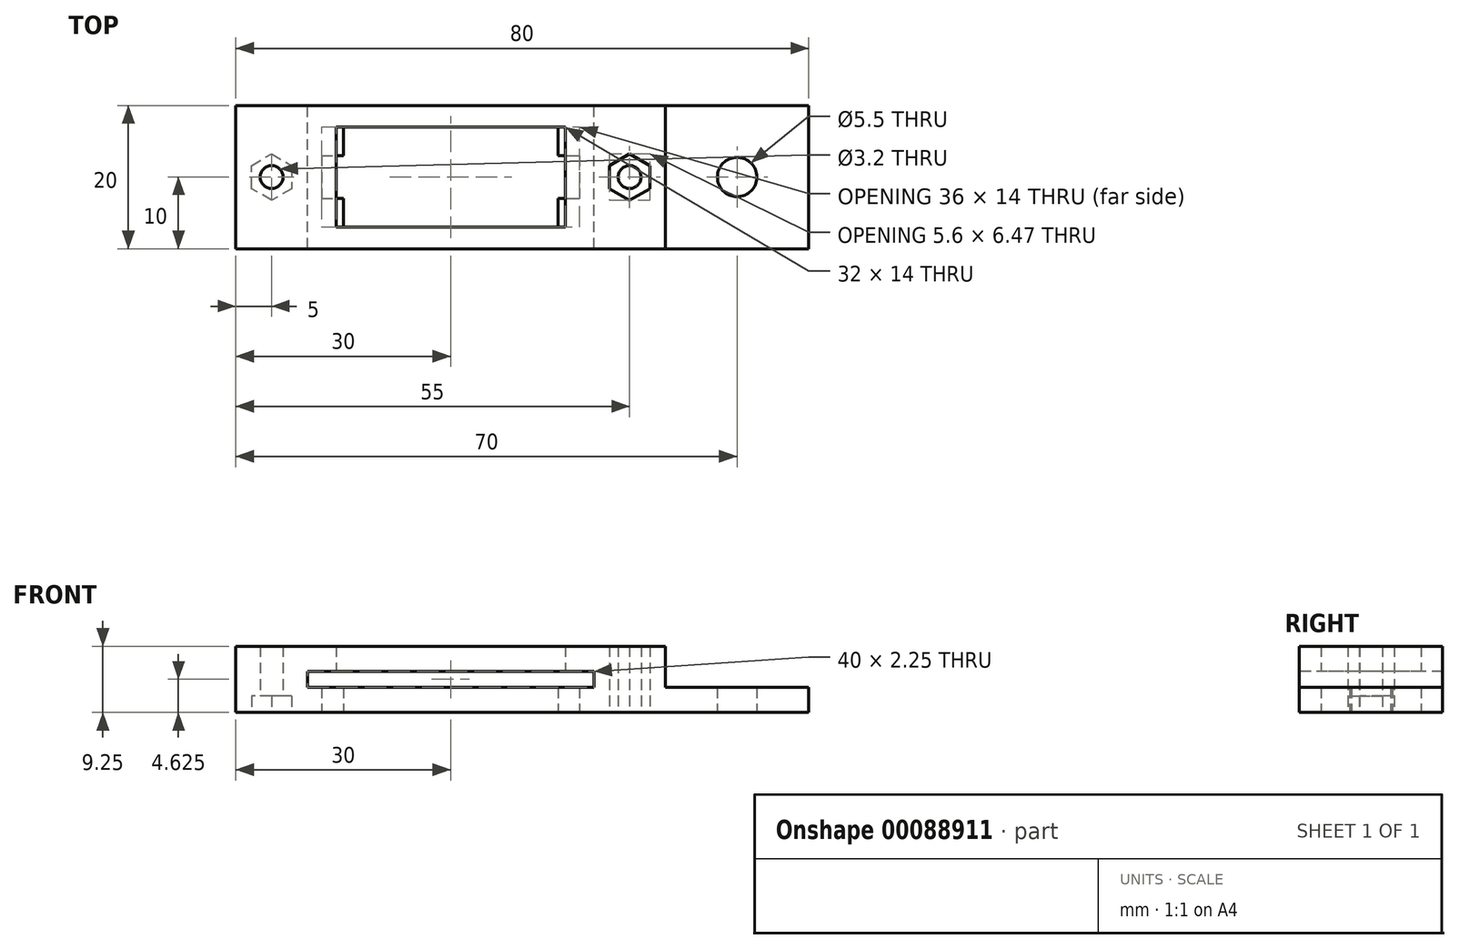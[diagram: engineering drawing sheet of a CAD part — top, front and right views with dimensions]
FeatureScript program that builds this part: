
annotation { "Feature Type Name" : "Feature", "Feature Type Description" : "" }
export const myFeature = defineFeature(function(context is Context, id is Id, definition is map)
    precondition{}
    {
        {
            var Q0;
            Q0=qCreatedBy(makeId("Top.planeOp"),FACE);
            var sketch = newSketch(context, id + "F0", { "sketchPlane" : qUnion([Q0])});
            skLineSegment(sketch, "E0.bottom", {"start": v(0, 0) * mm, "end": v(80, 0) * mm});
            skLineSegment(sketch, "E0.top", {"start": v(0, 20) * mm, "end": v(80, 20) * mm});
            skLineSegment(sketch, "E0.left", {"start": v(0, 0) * mm, "end": v(0, 20) * mm});
            skLineSegment(sketch, "E0.right", {"start": v(80, 0) * mm, "end": v(80, 20) * mm});
            skLineSegment(sketch, "E1", {"start": v(60, 33.84) * mm, "end": v(60, -24.02) * mm, "construction": true});
            skLineSegment(sketch, "E2.bottom", {"start": v(15, 17) * mm, "end": v(45, 17) * mm});
            skLineSegment(sketch, "E2.top", {"start": v(15, 3) * mm, "end": v(45, 3) * mm});
            skLineSegment(sketch, "E2.left", {"start": v(15, 17) * mm, "end": v(15, 13) * mm});
            skLineSegment(sketch, "E2.right", {"start": v(45, 17) * mm, "end": v(45, 13) * mm});
            skLineSegment(sketch, "E3", {"start": v(-13.8, 10) * mm, "end": v(89.02, 10) * mm, "construction": true});
            skLineSegment(sketch, "E4", {"start": v(30, 46.98) * mm, "end": v(30, -23.4) * mm, "construction": true});
            skLineSegment(sketch, "E5.bottom", {"start": v(12, 13) * mm, "end": v(15, 13) * mm});
            skLineSegment(sketch, "E5.top", {"start": v(12, 7) * mm, "end": v(15, 7) * mm});
            skLineSegment(sketch, "E5.left", {"start": v(12, 13) * mm, "end": v(12, 7) * mm});
            skLineSegment(sketch, "E5.right", {"start": v(48, 13) * mm, "end": v(48, 7) * mm});
            skLineSegment(sketch, "E6.trimOffspring", {"start": v(15, 7) * mm, "end": v(15, 3) * mm});
            skLineSegment(sketch, "E7.trimOffspring", {"start": v(45, 13) * mm, "end": v(48, 13) * mm});
            skLineSegment(sketch, "E8.trimOffspring", {"start": v(45, 7) * mm, "end": v(48, 7) * mm});
            skLineSegment(sketch, "E9.trimOffspring", {"start": v(45, 7) * mm, "end": v(45, 3) * mm});
            skCircle(sketch, "E10", {"center": v(70, 10) * mm, "radius": 2.75 * mm});
            skLineSegment(sketch, "E11", {"start": v(70, 32.2) * mm, "end": v(70, -17.83) * mm, "construction": true});
            skSolve(sketch);
        }
        {
            var Q0;
            Q0 = qSketchRegion(id + "F0", true);
            extrude(context, id + "F1", {"entities" : qUnion([Q0]), "depth" : 3.5 * mm});
        }
        {
            var Q0;
            Q0=makeQuery(id+"F1.opExtrude","CAP_FACE",FACE,{"disambiguationData":[OSD([sQuery(id+"F0.wireOp",EDGE,"E0.bottom"),sQuery(id+"F0.wireOp",EDGE,"E0.top"),sQuery(id+"F0.wireOp",EDGE,"E0.left"),sQuery(id+"F0.wireOp",EDGE,"E0.right"),sQuery(id+"F0.wireOp",EDGE,"E2.bottom"),sQuery(id+"F0.wireOp",EDGE,"E2.top"),sQuery(id+"F0.wireOp",EDGE,"E2.left"),sQuery(id+"F0.wireOp",EDGE,"E2.right"),sQuery(id+"F0.wireOp",EDGE,"E5.bottom"),sQuery(id+"F0.wireOp",EDGE,"E5.top"),sQuery(id+"F0.wireOp",EDGE,"E5.left"),sQuery(id+"F0.wireOp",EDGE,"E5.right"),sQuery(id+"F0.wireOp",EDGE,"E6.trimOffspring"),sQuery(id+"F0.wireOp",EDGE,"E7.trimOffspring"),sQuery(id+"F0.wireOp",EDGE,"E8.trimOffspring"),sQuery(id+"F0.wireOp",EDGE,"E9.trimOffspring"),sQuery(id+"F0.wireOp",EDGE,"E10")])],"isStart":false});
            cPlane(context, id + "F2", {"entities" : qUnion([Q0]), "cplaneType" : CPlaneType.OFFSET, "offset" : 2.25 * mm, "width" : 150 * mm, "height" : 150 * mm});
        }
        {
            var Q0;
            Q0=qCreatedBy(id+"F2.planeOp",FACE);
            var sketch = newSketch(context, id + "F3", { "sketchPlane" : qUnion([Q0])});
            skLineSegment(sketch, "E12.bottom", {"start": v(0, 20) * mm, "end": v(60, 20) * mm});
            skLineSegment(sketch, "E12.top", {"start": v(0, 0) * mm, "end": v(60, 0) * mm});
            skLineSegment(sketch, "E12.left", {"start": v(0, 20) * mm, "end": v(0, 0) * mm});
            skLineSegment(sketch, "E12.right", {"start": v(60, 20) * mm, "end": v(60, 0) * mm});
            skLineSegment(sketch, "E13.bottom", {"start": v(14, 17) * mm, "end": v(46, 17) * mm});
            skLineSegment(sketch, "E13.top", {"start": v(14, 3) * mm, "end": v(46, 3) * mm});
            skLineSegment(sketch, "E13.left", {"start": v(14, 17) * mm, "end": v(14, 3) * mm});
            skLineSegment(sketch, "E13.right", {"start": v(46, 17) * mm, "end": v(46, 3) * mm});
            skSolve(sketch);
        }
        {
            var Q0;
            Q0 = qSketchRegion(id + "F3", true);
            extrude(context, id + "F4", {"entities" : qUnion([Q0]), "depth" : 3.5 * mm});
        }
        {
            var Q0;
            Q0=makeQuery(id+"F4.opExtrude","CAP_FACE",FACE,{"disambiguationData":[OSD([sQuery(id+"F3.wireOp",EDGE,"E12.bottom"),sQuery(id+"F3.wireOp",EDGE,"E12.top"),sQuery(id+"F3.wireOp",EDGE,"E12.left"),sQuery(id+"F3.wireOp",EDGE,"E12.right"),sQuery(id+"F3.wireOp",EDGE,"E13.bottom"),sQuery(id+"F3.wireOp",EDGE,"E13.top"),sQuery(id+"F3.wireOp",EDGE,"E13.left"),sQuery(id+"F3.wireOp",EDGE,"E13.right")])],"isStart":false});
            var sketch = newSketch(context, id + "F5", { "sketchPlane" : qUnion([Q0])});
            skLineSegment(sketch, "E14.bottom", {"start": v(0, 20) * mm, "end": v(10, 20) * mm});
            skLineSegment(sketch, "E14.top", {"start": v(0, 0) * mm, "end": v(10, 0) * mm});
            skLineSegment(sketch, "E14.left", {"start": v(0, 20) * mm, "end": v(0, 0) * mm});
            skLineSegment(sketch, "E14.right", {"start": v(10, 20) * mm, "end": v(10, 0) * mm});
            skLineSegment(sketch, "E15.MirrorCS", {"start": v(60, 20) * mm, "end": v(50, 20) * mm});
            skLineSegment(sketch, "E16.MirrorCS", {"start": v(60, 0) * mm, "end": v(50, 0) * mm});
            skLineSegment(sketch, "E17.MirrorCS", {"start": v(50, 20) * mm, "end": v(50, 0) * mm});
            skLineSegment(sketch, "E18.MirrorCS", {"start": v(60, 20) * mm, "end": v(60, 0) * mm});
            skSolve(sketch);
        }
        {
            var Q0;
            Q0 = qSketchRegion(id + "F5", true);
            var Q1;
            Q1=makeQuery(id+"F1.opExtrude","CAP_FACE",FACE,{"disambiguationData":[OSD([sQuery(id+"F0.wireOp",EDGE,"E0.bottom"),sQuery(id+"F0.wireOp",EDGE,"E0.top"),sQuery(id+"F0.wireOp",EDGE,"E0.left"),sQuery(id+"F0.wireOp",EDGE,"E0.right"),sQuery(id+"F0.wireOp",EDGE,"E2.bottom"),sQuery(id+"F0.wireOp",EDGE,"E2.top"),sQuery(id+"F0.wireOp",EDGE,"E2.left"),sQuery(id+"F0.wireOp",EDGE,"E2.right"),sQuery(id+"F0.wireOp",EDGE,"E5.bottom"),sQuery(id+"F0.wireOp",EDGE,"E5.top"),sQuery(id+"F0.wireOp",EDGE,"E5.left"),sQuery(id+"F0.wireOp",EDGE,"E5.right"),sQuery(id+"F0.wireOp",EDGE,"E6.trimOffspring"),sQuery(id+"F0.wireOp",EDGE,"E7.trimOffspring"),sQuery(id+"F0.wireOp",EDGE,"E8.trimOffspring"),sQuery(id+"F0.wireOp",EDGE,"E9.trimOffspring"),sQuery(id+"F0.wireOp",EDGE,"E10")])],"isStart":false});
            extrude(context, id + "F6", {"entities" : qUnion([Q0]), "operationType" : NewBodyOperationType.ADD, "endBound" : BoundingType.UP_TO_SURFACE, "oppositeDirection" : true, "endBoundEntityFace" : qUnion([Q1]), "depth" : 25 * mm});
        }
        {
            var Q0;
            Q0=makeQuery(id+"F0.imprint","IMPRINT",FACE,{"disambiguationData":[TD([[makeQuery(id+"F0.imprint","IMPRINT",EDGE,{"derivedFrom":sQuery(id+"F0.wireOp",EDGE,"E0.bottom")}),1.0]])]});
            var sketch = newSketch(context, id + "F7", { "sketchPlane" : qUnion([Q0])});
            skCircle(sketch, "E19", {"center": v(5, 10) * mm, "radius": 1.6 * mm});
            skCircle(sketch, "E20.cCircle", {"center": v(5, 10) * mm, "radius": 2.8 * mm, "construction": true});
            skLineSegment(sketch, "E20.0", {"start": v(2.2, 8.38) * mm, "end": v(2.2, 11.62) * mm});
            skLineSegment(sketch, "E20.1", {"start": v(2.2, 11.62) * mm, "end": v(5, 13.23) * mm});
            skLineSegment(sketch, "E20.2", {"start": v(5, 13.23) * mm, "end": v(7.8, 11.62) * mm});
            skLineSegment(sketch, "E20.3", {"start": v(7.8, 11.62) * mm, "end": v(7.8, 8.38) * mm});
            skLineSegment(sketch, "E20.4", {"start": v(7.8, 8.38) * mm, "end": v(5, 6.77) * mm});
            skLineSegment(sketch, "E20.5", {"start": v(5, 6.77) * mm, "end": v(2.2, 8.38) * mm});
            skPoint(sketch, "E20.0.midPoint", {"position": v(2.2, 10) * mm});
            skLineSegment(sketch, "E21", {"start": v(5, -4.7) * mm, "end": v(5, 22.62) * mm, "construction": true});
            skLineSegment(sketch, "E22.MirrorCS", {"start": v(57.8, 8.38) * mm, "end": v(57.8, 11.62) * mm});
            skLineSegment(sketch, "E23.MirrorCS", {"start": v(55, 6.77) * mm, "end": v(57.8, 8.38) * mm});
            skLineSegment(sketch, "E24.MirrorCS", {"start": v(52.2, 8.38) * mm, "end": v(55, 6.77) * mm});
            skLineSegment(sketch, "E25.MirrorCS", {"start": v(52.2, 11.62) * mm, "end": v(52.2, 8.38) * mm});
            skLineSegment(sketch, "E26.MirrorCS", {"start": v(57.8, 11.62) * mm, "end": v(55, 13.23) * mm});
            skLineSegment(sketch, "E27.MirrorCS", {"start": v(55, 13.23) * mm, "end": v(52.2, 11.62) * mm});
            skCircle(sketch, "E28.MirrorC", {"center": v(55, 10) * mm, "radius": 2.8 * mm, "construction": true});
            skCircle(sketch, "E29.MirrorC", {"center": v(55, 10) * mm, "radius": 1.6 * mm});
            skPoint(sketch, "E30.MirrorP", {"position": v(57.8, 10) * mm});
            skSolve(sketch);
        }
        {
            var Q0;
            Q0=makeQuery(id+"F7.imprint","IMPRINT",FACE,{"disambiguationData":[TD([[makeQuery(id+"F7.imprint","IMPRINT",EDGE,{"derivedFrom":sQuery(id+"F7.wireOp",EDGE,"E19")}),1.0]])]});
            var Q1;
            Q1=makeQuery(id+"F7.imprint","IMPRINT",FACE,{"disambiguationData":[TD([[makeQuery(id+"F7.imprint","IMPRINT",EDGE,{"derivedFrom":sQuery(id+"F7.wireOp",EDGE,"E29.MirrorC")}),-1.0]])]});
            extrude(context, id + "F8", {"entities" : qUnion([Q0, Q1]), "operationType" : NewBodyOperationType.REMOVE, "endBound" : BoundingType.THROUGH_ALL, "depth" : 25 * mm});
        }
        {
            var Q0;
            Q0=makeQuery(id+"F7.imprint","IMPRINT",FACE,{"disambiguationData":[TD([[makeQuery(id+"F7.imprint","IMPRINT",EDGE,{"derivedFrom":sQuery(id+"F7.wireOp",EDGE,"E19")}),-1.0]])]});
            var Q1;
            Q1=makeQuery(id+"F7.imprint","IMPRINT",FACE,{"disambiguationData":[TD([[makeQuery(id+"F7.imprint","IMPRINT",EDGE,{"derivedFrom":sQuery(id+"F7.wireOp",EDGE,"E22.MirrorCS")}),1.0]])]});
            extrude(context, id + "F9", {"entities" : qUnion([Q0, Q1]), "operationType" : NewBodyOperationType.REMOVE, "depth" : 2.3 * mm});
        }
    });
